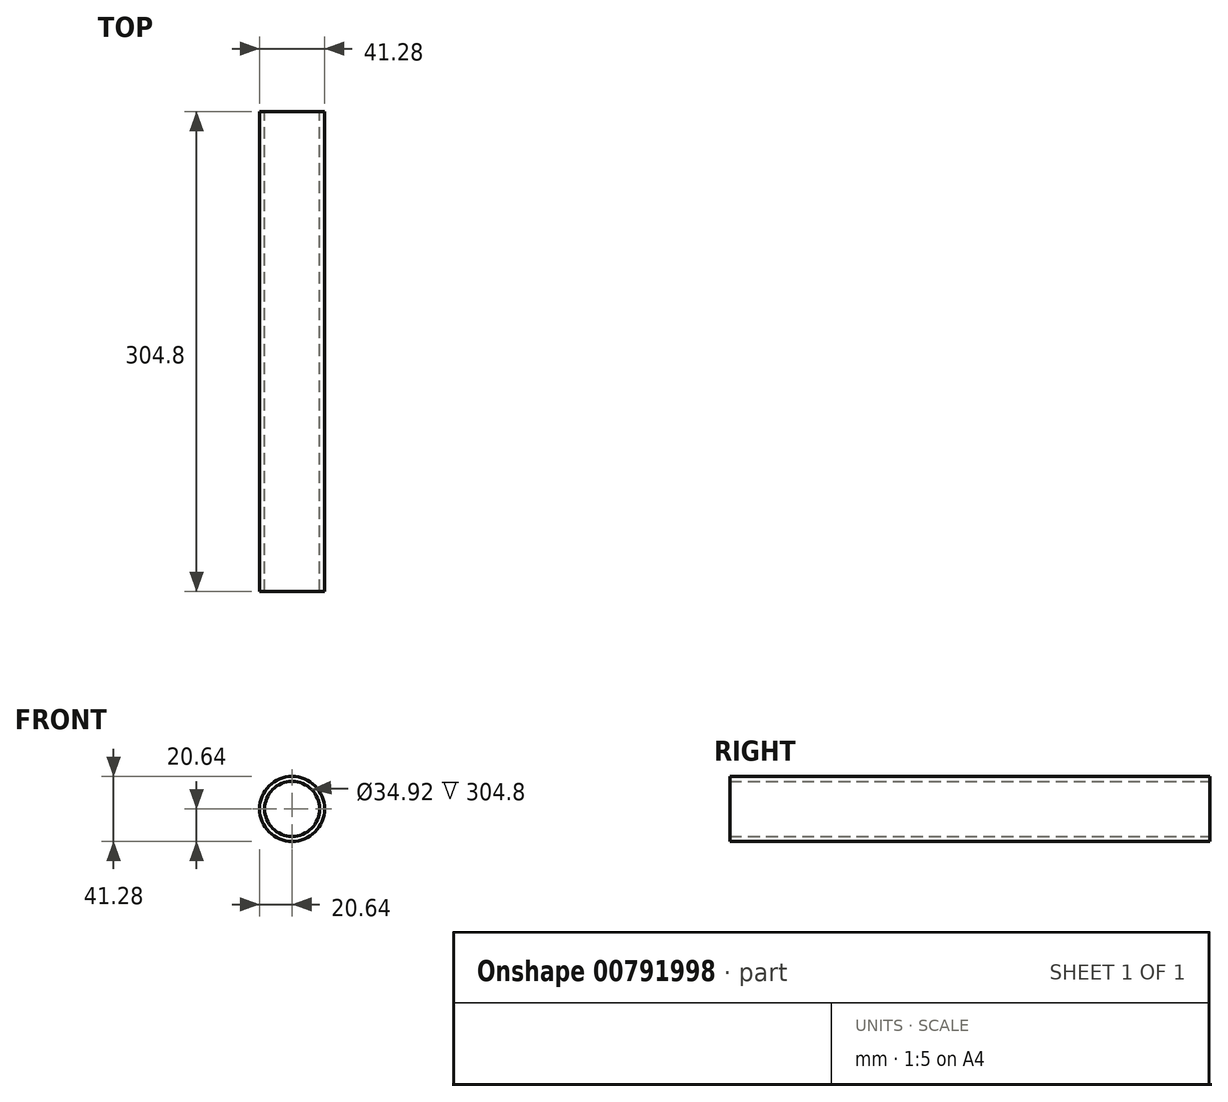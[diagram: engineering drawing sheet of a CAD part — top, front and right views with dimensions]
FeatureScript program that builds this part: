
annotation { "Feature Type Name" : "Feature", "Feature Type Description" : "" }
export const myFeature = defineFeature(function(context is Context, id is Id, definition is map)
    precondition{}
    {
        {
            assignVariable(context, id + "F0", {"name" : "length", "anyValue" : 304.8 * mm});
        }
        {
            var Q0;
            Q0=qCreatedBy(makeId("Front.planeOp"),FACE);
            var sketch = newSketch(context, id + "F1", { "sketchPlane" : qUnion([Q0])});
            skCircle(sketch, "E0", {"center": v(0, 0) * mm, "radius": 20.64 * mm});
            skCircle(sketch, "E1", {"center": v(0, 0) * mm, "radius": 17.46 * mm});
            skSolve(sketch);
        }
        {
            var Q0;
            Q0 = qSketchRegion(id + "F1", true);
            extrude(context, id + "F2", {"entities" : qUnion([Q0]), "depth" : getVariable(context, 'length'), "offsetDistance" : 25.4 * mm});
        }
    });
